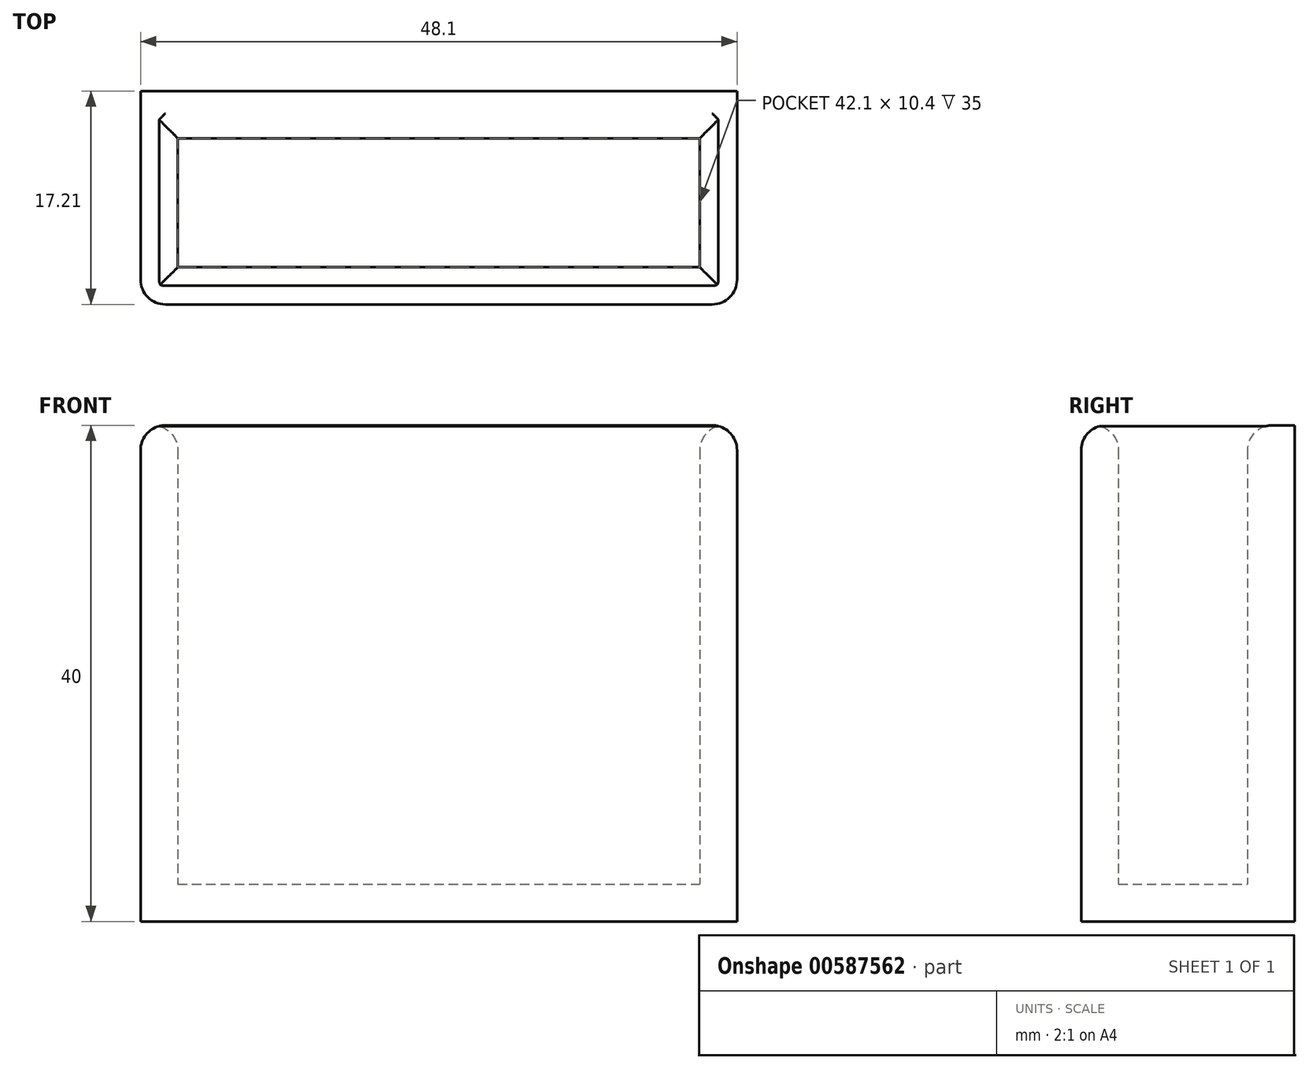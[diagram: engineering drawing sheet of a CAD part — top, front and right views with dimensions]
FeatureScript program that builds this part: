
annotation { "Feature Type Name" : "Feature", "Feature Type Description" : "" }
export const myFeature = defineFeature(function(context is Context, id is Id, definition is map)
    precondition{}
    {
        {
            var Q0;
            Q0=qCreatedBy(makeId("Front.planeOp"),FACE);
            var sketch = newSketch(context, id + "F0", { "sketchPlane" : qUnion([Q0])});
            skLineSegment(sketch, "E0.bottom", {"start": v(14.05, 62.1) * mm, "end": v(-14.05, 62.1) * mm});
            skLineSegment(sketch, "E0.top", {"start": v(14.05, -62.1) * mm, "end": v(-14.05, -62.1) * mm});
            skLineSegment(sketch, "E0.left", {"start": v(19.05, 57.1) * mm, "end": v(19.05, -57.1) * mm});
            skLineSegment(sketch, "E0.right", {"start": v(-19.05, 57.1) * mm, "end": v(-19.05, -57.1) * mm});
            skPoint(sketch, "E0.middle", {"position": v(0, 0) * mm});
            skPoint(sketch, "E1.visualSharp", {"position": v(19.05, 62.1) * mm});
            skArc(sketch, "E1.filletArc", {"start": v(19.05, 57.1) * mm, "mid": v(17.59, 60.64) * mm, "end": v(14.05, 62.1) * mm});
            skPoint(sketch, "E2.visualSharp", {"position": v(19.05, -62.1) * mm});
            skArc(sketch, "E2.filletArc", {"start": v(14.05, -62.1) * mm, "mid": v(17.59, -60.64) * mm, "end": v(19.05, -57.1) * mm});
            skPoint(sketch, "E3.visualSharp", {"position": v(-19.05, -62.1) * mm});
            skArc(sketch, "E3.filletArc", {"start": v(-19.05, -57.1) * mm, "mid": v(-17.59, -60.64) * mm, "end": v(-14.05, -62.1) * mm});
            skPoint(sketch, "E4.visualSharp", {"position": v(-19.05, 62.1) * mm});
            skArc(sketch, "E4.filletArc", {"start": v(-14.05, 62.1) * mm, "mid": v(-17.59, 60.64) * mm, "end": v(-19.05, 57.1) * mm});
            skSolve(sketch);
        }
        {
            var Q0;
            Q0=qSketchRegion(id+"F0",true);
            extrude(context, id + "F1", {"entities" : qUnion([Q0]), "depth" : 6.4 * mm});
        }
        {
            var Q0;
            Q0=makeQuery(id+"F1.opExtrude","CAP_FACE",FACE,{"disambiguationData":[OSD([sQuery(id+"F0.wireOp",EDGE,"E0.bottom"),sQuery(id+"F0.wireOp",EDGE,"E0.top"),sQuery(id+"F0.wireOp",EDGE,"E0.left"),sQuery(id+"F0.wireOp",EDGE,"E0.right"),sQuery(id+"F0.wireOp",EDGE,"E1.filletArc"),sQuery(id+"F0.wireOp",EDGE,"E2.filletArc"),sQuery(id+"F0.wireOp",EDGE,"E3.filletArc"),sQuery(id+"F0.wireOp",EDGE,"E4.filletArc")])],"isStart":false});
            var sketch = newSketch(context, id + "F2", { "sketchPlane" : qUnion([Q0])});
            skLineSegment(sketch, "E5", {"start": v(0, 62.1) * mm, "end": v(0, -62.1) * mm, "construction": true});
            skLineSegment(sketch, "E6", {"start": v(8, 62.1) * mm, "end": v(8, -62.1) * mm, "construction": true});
            skLineSegment(sketch, "E7", {"start": v(-19.05, 0) * mm, "end": v(19.05, 0) * mm, "construction": true});
            skLineSegment(sketch, "E8", {"start": v(-19.05, 16.1) * mm, "end": v(19.05, 16.1) * mm, "construction": true});
            skCircle(sketch, "E9", {"center": v(8, 0) * mm, "radius": 6.4 * mm});
            skCircle(sketch, "E10", {"center": v(8, 16.1) * mm, "radius": 6.4 * mm});
            skCircle(sketch, "E11.MirrorC", {"center": v(8, -16.1) * mm, "radius": 6.4 * mm});
            skCircle(sketch, "E12.MirrorC", {"center": v(-8, 16.1) * mm, "radius": 6.4 * mm});
            skCircle(sketch, "E13.MirrorC", {"center": v(-8, 0) * mm, "radius": 6.4 * mm});
            skCircle(sketch, "E14.MirrorC", {"center": v(-8, -16.1) * mm, "radius": 6.4 * mm});
            skLineSegment(sketch, "E15", {"start": v(1.6, 0) * mm, "end": v(1.6, -16.1) * mm});
            skLineSegment(sketch, "E16", {"start": v(14.4, 0) * mm, "end": v(14.4, -16.1) * mm});
            skSolve(sketch);
        }
        {
            var Q0;
            Q0=qSketchRegion(id+"F2",true);
            extrude(context, id + "F3", {"entities" : qUnion([Q0]), "operationType" : NewBodyOperationType.ADD, "depth" : .5 * mm});
        }
        {
            var Q0;
            Q0=makeQuery(id+"F1.opExtrude","SWEPT_FACE",FACE,{"disambiguationData":[OSD([sQuery(id+"F0.wireOp",EDGE,"E0.top")])]});
            var sketch = newSketch(context, id + "F4", { "sketchPlane" : qUnion([Q0])});
            skLineSegment(sketch, "E17.0", {"start": v(-24.05, 11.4) * mm, "end": v(-14.05, 11.4) * mm});
            skLineSegment(sketch, "E17.1", {"start": v(14.05, 11.4) * mm, "end": v(-14.05, 11.4) * mm});
            skLineSegment(sketch, "E17.2", {"start": v(-24.05, 11.4) * mm, "end": v(-24.05, -5) * mm});
            skLineSegment(sketch, "E17.3", {"start": v(14.05, 11.4) * mm, "end": v(24.05, 11.4) * mm});
            skLineSegment(sketch, "E17.4", {"start": v(-24.05, -5) * mm, "end": v(-14.05, -5) * mm});
            skLineSegment(sketch, "E17.5", {"start": v(14.05, -5) * mm, "end": v(-14.05, -5) * mm});
            skLineSegment(sketch, "E17.6", {"start": v(14.05, -5) * mm, "end": v(24.05, -5) * mm});
            skLineSegment(sketch, "E17.7", {"start": v(24.05, 11.4) * mm, "end": v(24.05, -5) * mm});
            skSolve(sketch);
        }
        {
            var Q0;
            Q0=qSketchRegion(id+"F4",true);
            extrude(context, id + "F5", {"entities" : qUnion([Q0]), "oppositeDirection" : true, "depth" : 35 * mm, "hasSecondDirection" : true, "secondDirectionOppositeDirection" : false, "secondDirectionDepth" : 5 * mm});
        }
        {
            var Q0;
            Q0=makeQuery(id+"F5.opExtrude","CAP_FACE",FACE,{"disambiguationData":[OSD([sQuery(id+"F4.wireOp",EDGE,"E17.0"),sQuery(id+"F4.wireOp",EDGE,"E17.1"),sQuery(id+"F4.wireOp",EDGE,"E17.2"),sQuery(id+"F4.wireOp",EDGE,"E17.3"),sQuery(id+"F4.wireOp",EDGE,"E17.4"),sQuery(id+"F4.wireOp",EDGE,"E17.5"),sQuery(id+"F4.wireOp",EDGE,"E17.6"),sQuery(id+"F4.wireOp",EDGE,"E17.7")])],"isStart":false});
            shell(context, id + "F6", {"entities" : qUnion([Q0]), "thickness" : 3 * mm});
        }
        {
            var Q0;
            Q0=makeQuery(id+"F5.opExtrude","SWEPT_FACE",FACE,{"disambiguationData":[OSD([sQuery(id+"F4.wireOp",EDGE,"E17.4"),sQuery(id+"F4.wireOp",EDGE,"E17.5"),sQuery(id+"F4.wireOp",EDGE,"E17.6")])]});
            var sketch = newSketch(context, id + "F7", { "sketchPlane" : qUnion([Q0])});
            skSolve(sketch);
        }
        {
            var Q0;
            {var subQ0=sQuery(id+"F4.wireOp",EDGE,"E17.4");Q0=makeQuery(id+"F7.imprint","IMPRINT",FACE,{"disambiguationData":[TD([[makeQuery(id+"F7.imprint","IMPRINT",EDGE,{"derivedFrom":makeQuery(id+"F5.opExtrude","SWEPT_EDGE",EDGE,{"disambiguationData":[OSD([sQuery(id+"F4.wireOp",EDGE,"E17.2"),subQ0])]})}),-1.0]])]});}
            extrude(context, id + "F8", {"entities" : qUnion([Q0]), "operationType" : NewBodyOperationType.ADD, "depth" : 10 * mm});
        }
        {
            var Q0;
            {var subQ0=sQuery(id+"F4.wireOp",EDGE,"E17.6");var subQ1=sQuery(id+"F4.wireOp",EDGE,"E17.5");var subQ2=sQuery(id+"F4.wireOp",EDGE,"E17.4");Q0=makeQuery(id+"F8.boolean.opBoolean","MERGE",FACE,{"derivedFrom":[makeQuery(id+"F5.opExtrude","CAP_FACE",FACE,{"disambiguationData":[OSD([sQuery(id+"F4.wireOp",EDGE,"E17.0"),sQuery(id+"F4.wireOp",EDGE,"E17.1"),sQuery(id+"F4.wireOp",EDGE,"E17.2"),sQuery(id+"F4.wireOp",EDGE,"E17.3"),subQ2,subQ1,subQ0,sQuery(id+"F4.wireOp",EDGE,"E17.7")])],"isStart":false}),makeQuery(id+"F8.opExtrude","SWEPT_FACE",FACE,{"disambiguationData":[OSD([subQ2,subQ1,subQ0]),TDD([makeQuery(id+"F7.imprint","IMPRINT",EDGE,{"derivedFrom":makeQuery(id+"F5.opExtrude","CAP_EDGE",EDGE,{"disambiguationData":[OSD([subQ2,subQ1,subQ0])],"isStart":false})})])]})]});}
            var Q1;
            Q1=makeQuery(id+"F5.opExtrude","SWEPT_EDGE",EDGE,{"disambiguationData":[OSD([sQuery(id+"F4.wireOp",EDGE,"E17.3"),sQuery(id+"F4.wireOp",EDGE,"E17.7")])]});
            var Q2;
            Q2=makeQuery(id+"F8.opExtrude","CAP_EDGE",EDGE,{"disambiguationData":[OSD([sQuery(id+"F4.wireOp",EDGE,"E17.6"),sQuery(id+"F4.wireOp",EDGE,"E17.7")])],"isStart":false});
            var Q3;
            Q3=makeQuery(id+"F8.opExtrude","CAP_EDGE",EDGE,{"disambiguationData":[OSD([sQuery(id+"F4.wireOp",EDGE,"E17.2"),sQuery(id+"F4.wireOp",EDGE,"E17.4")])],"isStart":false});
            var Q4;
            Q4=makeQuery(id+"F5.opExtrude","SWEPT_EDGE",EDGE,{"disambiguationData":[OSD([sQuery(id+"F4.wireOp",EDGE,"E17.0"),sQuery(id+"F4.wireOp",EDGE,"E17.2")])]});
            fillet(context, id + "F9", {"entities" : qUnion([Q0, Q1, Q2, Q3, Q4]), "radius" : 2 * mm, "tangentPropagation" : true, "allowEdgeOverflow" : false});
        }
        {
            var Q0;
            Q0=makeQuery(id+"F1.opExtrude","SWEPT_BODY",BODY,{"disambiguationData":[OSD([sQuery(id+"F0.wireOp",EDGE,"E0.bottom"),sQuery(id+"F0.wireOp",EDGE,"E0.top"),sQuery(id+"F0.wireOp",EDGE,"E0.left"),sQuery(id+"F0.wireOp",EDGE,"E0.right"),sQuery(id+"F0.wireOp",EDGE,"E1.filletArc"),sQuery(id+"F0.wireOp",EDGE,"E2.filletArc"),sQuery(id+"F0.wireOp",EDGE,"E3.filletArc"),sQuery(id+"F0.wireOp",EDGE,"E4.filletArc")])]});
            deleteBodies(context, id + "F10", {"entities" : qUnion([Q0])});
        }
        {
            var Q0;
            {var subQ0=sQuery(id+"F4.wireOp",EDGE,"E17.6");var subQ1=sQuery(id+"F4.wireOp",EDGE,"E17.5");var subQ2=sQuery(id+"F4.wireOp",EDGE,"E17.4");Q0=makeQuery(id+"F8.boolean.opBoolean","MERGE",FACE,{"derivedFrom":[makeQuery(id+"F5.opExtrude","CAP_FACE",FACE,{"disambiguationData":[OSD([sQuery(id+"F4.wireOp",EDGE,"E17.0"),sQuery(id+"F4.wireOp",EDGE,"E17.1"),sQuery(id+"F4.wireOp",EDGE,"E17.2"),sQuery(id+"F4.wireOp",EDGE,"E17.3"),subQ2,subQ1,subQ0,sQuery(id+"F4.wireOp",EDGE,"E17.7")])],"isStart":false}),makeQuery(id+"F8.opExtrude","SWEPT_FACE",FACE,{"disambiguationData":[OSD([subQ2,subQ1,subQ0]),TDD([makeQuery(id+"F7.imprint","IMPRINT",EDGE,{"derivedFrom":makeQuery(id+"F5.opExtrude","CAP_EDGE",EDGE,{"disambiguationData":[OSD([subQ2,subQ1,subQ0])],"isStart":false})})])]})]});}
            var sketch = newSketch(context, id + "F11", { "sketchPlane" : qUnion([Q0])});
            skLineSegment(sketch, "E18.bottom", {"start": v(-33.18, 5.81) * mm, "end": v(32.45, 5.81) * mm});
            skLineSegment(sketch, "E18.top", {"start": v(-33.18, 20.48) * mm, "end": v(32.45, 20.48) * mm});
            skLineSegment(sketch, "E18.left", {"start": v(-33.18, 5.81) * mm, "end": v(-33.18, 20.48) * mm});
            skLineSegment(sketch, "E18.right", {"start": v(32.45, 5.81) * mm, "end": v(32.45, 20.48) * mm});
            skSolve(sketch);
        }
        {
            var Q0;
            Q0 = qSketchRegion(id + "F11", true);
            extrude(context, id + "F12", {"entities" : qUnion([Q0]), "operationType" : NewBodyOperationType.REMOVE, "endBound" : BoundingType.THROUGH_ALL, "oppositeDirection" : true, "depth" : 25 * mm, "offsetDistance" : 25 * mm});
        }
    });
